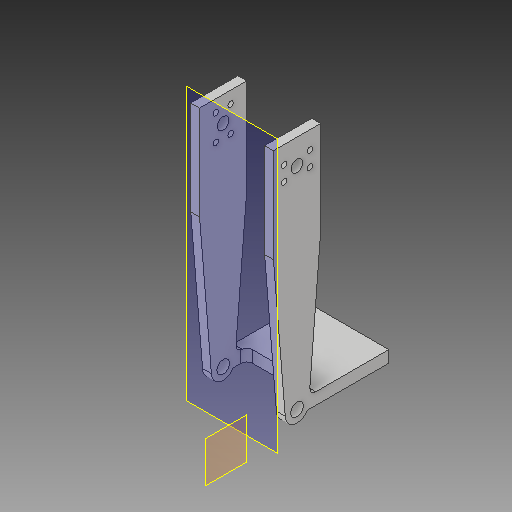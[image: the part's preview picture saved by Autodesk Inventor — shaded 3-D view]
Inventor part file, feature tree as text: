
AUTODESK INVENTOR PART (.ipt)
format: ipt  version: 2017 (Build 210142000, 142)  size: 268,800 bytes
history: native  units: in
note: dims shown in document units (in); Inventor stores cm internally (conversion verified against a paired STEP export)
features: sketch x9, projected_geometry x9, hole x5, extrude x4, plane x3, fillet x2, mirror x1
ambient origin geometry x8: Origin, YZ Plane, XZ Plane, XY Plane, X Axis, Y Axis, Z Axis, Center Point
bodies: Solid1 (feature_tree)
feature tree (33):
  sketch  "Sketch1"  dims[d0=5.0in d1=1.0in]
  plane  "Work Plane1"
  extrude  "Extrusion2"  Depth=1.0in
  plane  "Work Plane2"
  extrude  "Extrusion3"  Depth=1.0in
  hole  "Hole2"  [1 undecoded]
  extrude  "Extrusion4"  Depth=1.753in
  extrude  "Extrusion5"  Depth=1.753in
  fillet  "Fillet1"  Radius=2.0in
  fillet  "Fillet2"  Radius=1.753in
  hole  "Hole3"  [1 undecoded]
  hole  "Hole4"  [1 undecoded]
  hole  "Hole5"  [1 undecoded]
  hole  "Hole6"  [1 undecoded]
  plane  "Work Plane3"
  mirror  "Mirror1"
  sketch  "Sketch2"  dims[d5=1.0in d6=0.5in]
  projected_geometry  "Projected Loop1"
  sketch  "Sketch4"  dims[d7=0.5in d8=0.0in]
  projected_geometry  "Projected Loop3"
  sketch  "Sketch5"  dims[d9=1.753in d10=0.0in d18=0.5in]
  projected_geometry  "Projected Loop4"
  sketch  "Sketch8"  dims[d19=0.25in d20=2.0in d21=2.0in d22=1.753in d23=0.0in]
  projected_geometry  "Projected Loop9"
  projected_geometry  "Projected Loop10"
  sketch  "Sketch9"  dims[d24=0.27in d25=0.75in d26=0.375in d27=0.25in d28=0.5635in d29=1.0in d30=0.8108in d31=1.75in]
  projected_geometry  "Projected Loop11"
  sketch  "Sketch10"  dims[d32=0.25in d35=5.0in]
  projected_geometry  "Projected Loop12"
  sketch  "Sketch11"  dims[d36=4.875in d37=1.753in d38=0.0in]
  projected_geometry  "Projected Loop13"
  sketch  "Sketch12"  dims[d41=1.753in d42=5.375in d43=1.378in d44=0.1875in d45=5.875in d46=1.0in d47=0.0in d48=0.125in d49=0.125in d50=0.6299in d51=1.0in d52=0.5in d55=0.117in d56=0.75in d57=0.375in d58=0.25in d59=0.5635in d60=1.0in d61=0.8108in d62=0.6299in d63=1.0in d64=0.5in d67=0.117in d68=0.75in d69=0.375in d70=0.25in d71=0.5635in d72=1.0in d73=0.8108in d74=0.32in d75=1.753in d77=0.5in d78=0.75in d79=0.375in d80=0.25in d81=0.5635in d82=0.125in d83=0.0in d84=1.0in d85=0.5in d86=0.315in d87=0.1575in d88=0.25in d89=0.75in d90=0.375in d91=0.25in d92=0.5635in d93=1.0in d94=0.8108in d95=0.27in d96=0.1975in d97=0.375in d98=0.315in d99=0.1575in d100=0.53in d101=0.315in d102=0.1575in d103=0.53in]
  projected_geometry  "Projected Loop14"
note: 5 required parameter values undecoded (feature->parameter linkage not recoverable at this tier; creation-order binding heuristic only, values carry confidence <= 0.55)
